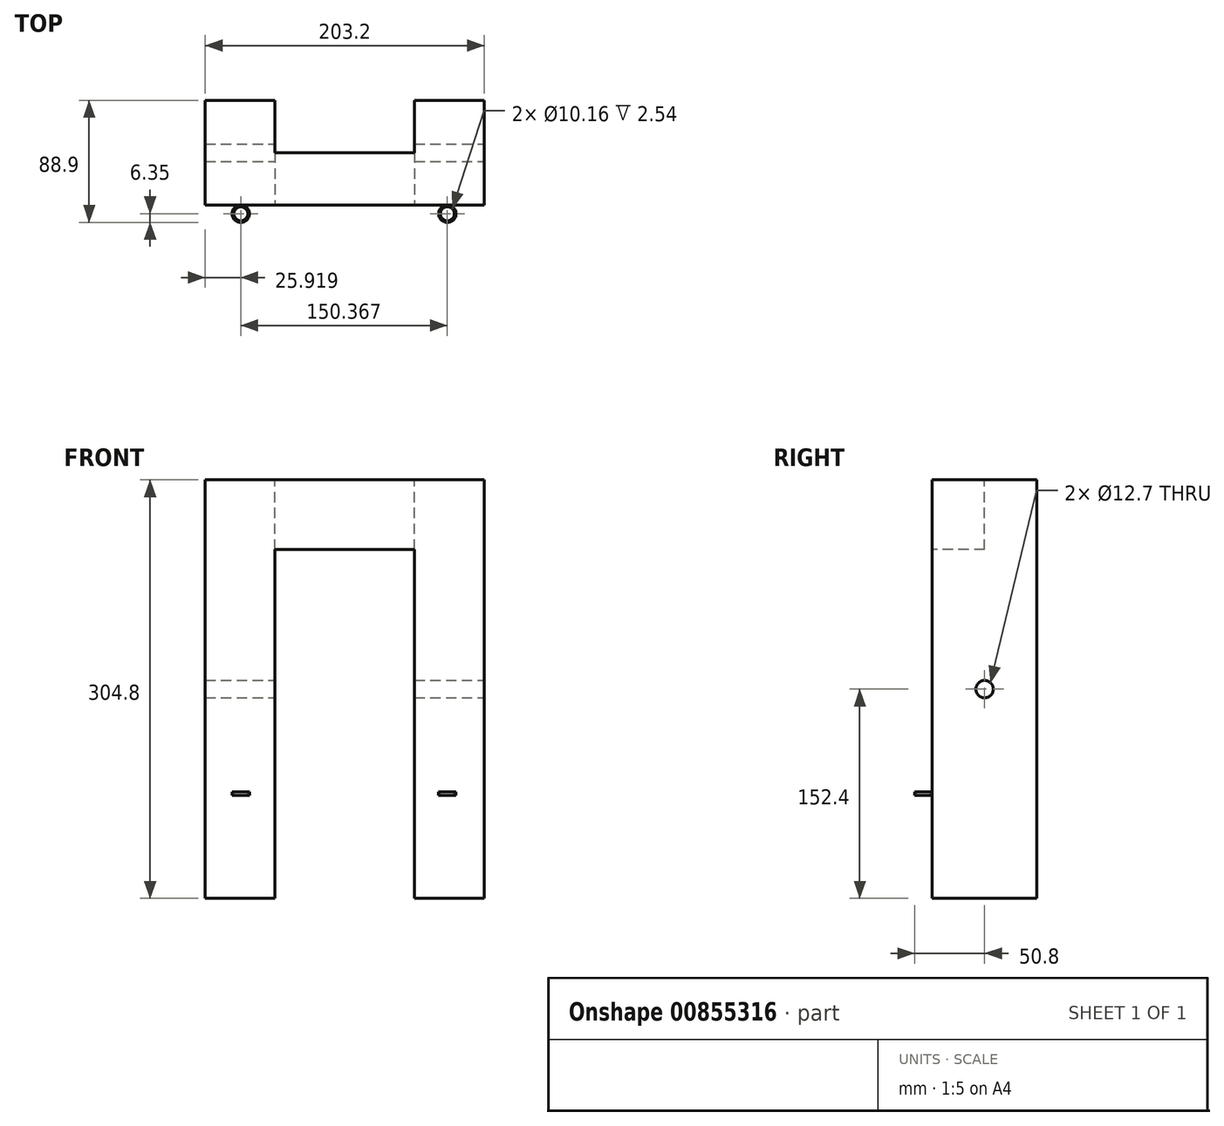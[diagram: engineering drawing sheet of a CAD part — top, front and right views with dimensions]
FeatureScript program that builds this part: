
annotation { "Feature Type Name" : "Feature", "Feature Type Description" : "" }
export const myFeature = defineFeature(function(context is Context, id is Id, definition is map)
    precondition{}
    {
        {
            var Q0;
            Q0=qCreatedBy(makeId("Top.planeOp"),FACE);
            var sketch = newSketch(context, id + "F0", { "sketchPlane" : qUnion([Q0])});
            skLineSegment(sketch, "E0.bottom", {"start": v(101.6, -38.1) * mm, "end": v(-101.6, -38.1) * mm});
            skLineSegment(sketch, "E0.top", {"start": v(101.6, 38.1) * mm, "end": v(-101.6, 38.1) * mm});
            skLineSegment(sketch, "E0.left", {"start": v(101.6, -38.1) * mm, "end": v(101.6, 38.1) * mm});
            skLineSegment(sketch, "E0.right", {"start": v(-101.6, -38.1) * mm, "end": v(-101.6, 38.1) * mm});
            skPoint(sketch, "E0.middle", {"position": v(0, 0) * mm});
            skSolve(sketch);
        }
        {
            var Q0;
            Q0 = qSketchRegion(id + "F0", true);
            extrude(context, id + "F1", {"entities" : qUnion([Q0]), "depth" : 304.8 * mm, "offsetDistance" : 25.4 * mm});
        }
        {
            var Q0;
            Q0=makeQuery(id+"F1.opExtrude","SWEPT_FACE",FACE,{"disambiguationData":[OSD([sQuery(id+"F0.wireOp",EDGE,"E0.bottom")])]});
            var sketch = newSketch(context, id + "F2", { "sketchPlane" : qUnion([Q0])});
            skLineSegment(sketch, "E1.bottom", {"start": v(50.8, 0) * mm, "end": v(-50.8, 0) * mm});
            skLineSegment(sketch, "E1.top", {"start": v(50.8, 254) * mm, "end": v(-50.8, 254) * mm});
            skLineSegment(sketch, "E1.left", {"start": v(50.8, 0) * mm, "end": v(50.8, 254) * mm});
            skLineSegment(sketch, "E1.right", {"start": v(-50.8, 0) * mm, "end": v(-50.8, 254) * mm});
            skPoint(sketch, "E1.middle", {"position": v(0, 127) * mm});
            skSolve(sketch);
        }
        {
            var Q0;
            Q0 = qSketchRegion(id + "F2", true);
            extrude(context, id + "F3", {"entities" : qUnion([Q0]), "operationType" : NewBodyOperationType.REMOVE, "endBound" : BoundingType.THROUGH_ALL, "oppositeDirection" : true, "depth" : 25.4 * mm, "offsetDistance" : 25.4 * mm});
        }
        {
            var Q0;
            Q0=makeQuery(id+"F1.opExtrude","SWEPT_FACE",FACE,{"disambiguationData":[OSD([sQuery(id+"F0.wireOp",EDGE,"E0.left")])]});
            var sketch = newSketch(context, id + "F4", { "sketchPlane" : qUnion([Q0])});
            skCircle(sketch, "E2", {"center": v(0, 152.4) * mm, "radius": 6.35 * mm});
            skSolve(sketch);
        }
        {
            var Q0;
            Q0 = qSketchRegion(id + "F4", true);
            extrude(context, id + "F5", {"entities" : qUnion([Q0]), "operationType" : NewBodyOperationType.REMOVE, "endBound" : BoundingType.THROUGH_ALL, "oppositeDirection" : true, "depth" : 25.4 * mm, "offsetDistance" : 25.4 * mm});
        }
        {
            var Q0;
            Q0=qCreatedBy(makeId("Top.planeOp"),FACE);
            cPlane(context, id + "F6", {"entities" : qUnion([Q0]), "cplaneType" : CPlaneType.OFFSET, "offset" : 76.2 * mm, "width" : 152.4 * mm, "height" : 152.4 * mm});
        }
        {
            var Q0;
            Q0=qCreatedBy(id+"F6.planeOp",FACE);
            var sketch = newSketch(context, id + "F7", { "sketchPlane" : qUnion([Q0])});
            skCircle(sketch, "E3", {"center": v(74.69, -44.45) * mm, "radius": 6.35 * mm});
            skCircle(sketch, "E4", {"center": v(-75.68, -44.45) * mm, "radius": 6.35 * mm});
            skSolve(sketch);
        }
        {
            var Q0;
            Q0 = qSketchRegion(id + "F7", true);
            extrude(context, id + "F8", {"entities" : qUnion([Q0]), "operationType" : NewBodyOperationType.ADD, "depth" : 1.27 * mm, "offsetDistance" : 25.4 * mm, "hasSecondDirection" : true, "secondDirectionOppositeDirection" : true, "secondDirectionDepth" : 1.27 * mm});
        }
        {
            var Q0;
            Q0=makeQuery(id+"F8.opExtrude","CAP_FACE",FACE,{"disambiguationData":[OSD([sQuery(id+"F7.wireOp",EDGE,"E3")])],"isStart":false});
            var sketch = newSketch(context, id + "F9", { "sketchPlane" : qUnion([Q0])});
            skCircle(sketch, "E5", {"center": v(74.69, -44.45) * mm, "radius": 5.08 * mm});
            skCircle(sketch, "E6", {"center": v(-75.68, -44.45) * mm, "radius": 5.08 * mm});
            skSolve(sketch);
        }
        {
            var Q0;
            Q0 = qSketchRegion(id + "F9", true);
            extrude(context, id + "F10", {"entities" : qUnion([Q0]), "operationType" : NewBodyOperationType.REMOVE, "endBound" : BoundingType.THROUGH_ALL, "oppositeDirection" : true, "depth" : 25.4 * mm, "offsetDistance" : 25.4 * mm});
        }
        {
            var Q0;
            Q0=makeQuery(id+"F1.opExtrude","CAP_FACE",FACE,{"disambiguationData":[OSD([sQuery(id+"F0.wireOp",EDGE,"E0.bottom"),sQuery(id+"F0.wireOp",EDGE,"E0.top"),sQuery(id+"F0.wireOp",EDGE,"E0.left"),sQuery(id+"F0.wireOp",EDGE,"E0.right")])],"isStart":false});
            var sketch = newSketch(context, id + "F11", { "sketchPlane" : qUnion([Q0])});
            skLineSegment(sketch, "E7.bottom", {"start": v(50.8, 0) * mm, "end": v(-50.8, 0) * mm});
            skLineSegment(sketch, "E7.top", {"start": v(50.8, 38.1) * mm, "end": v(-50.8, 38.1) * mm});
            skLineSegment(sketch, "E7.left", {"start": v(50.8, 0) * mm, "end": v(50.8, 38.1) * mm});
            skLineSegment(sketch, "E7.right", {"start": v(-50.8, 0) * mm, "end": v(-50.8, 38.1) * mm});
            skPoint(sketch, "E7.middle", {"position": v(0, 19.05) * mm});
            skSolve(sketch);
        }
        {
            var Q0;
            Q0 = qSketchRegion(id + "F11", true);
            extrude(context, id + "F12", {"entities" : qUnion([Q0]), "operationType" : NewBodyOperationType.REMOVE, "endBound" : BoundingType.THROUGH_ALL, "oppositeDirection" : true, "depth" : 25.4 * mm, "offsetDistance" : 25.4 * mm});
        }
    });
